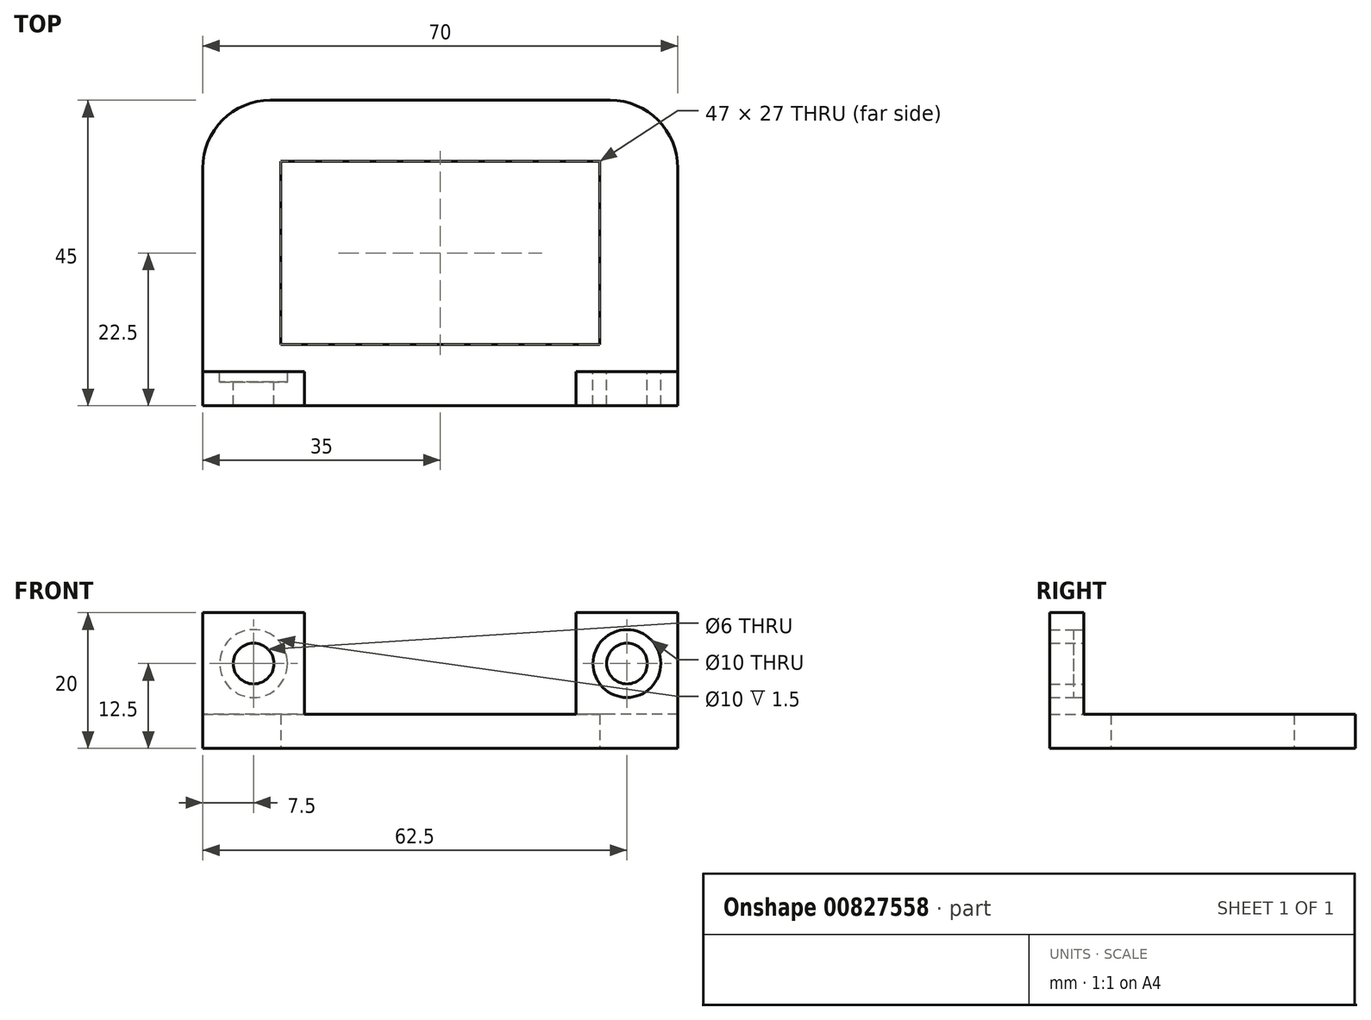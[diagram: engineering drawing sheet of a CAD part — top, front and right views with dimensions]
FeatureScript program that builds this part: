
annotation { "Feature Type Name" : "Feature", "Feature Type Description" : "" }
export const myFeature = defineFeature(function(context is Context, id is Id, definition is map)
    precondition{}
    {
        {
            var Q0;
            Q0=qCreatedBy(makeId("Top.planeOp"),FACE);
            var sketch = newSketch(context, id + "F0", { "sketchPlane" : qUnion([Q0])});
            skLineSegment(sketch, "E0.bottom", {"start": v(35, -22.5) * mm, "end": v(-35, -22.5) * mm});
            skLineSegment(sketch, "E0.top", {"start": v(25, 22.5) * mm, "end": v(-25, 22.5) * mm});
            skLineSegment(sketch, "E0.left", {"start": v(35, -22.5) * mm, "end": v(35, 12.5) * mm});
            skLineSegment(sketch, "E0.right", {"start": v(-35, -22.5) * mm, "end": v(-35, 12.5) * mm});
            skPoint(sketch, "E0.middle", {"position": v(0, 0) * mm});
            skPoint(sketch, "E1.visualSharp", {"position": v(35, 22.5) * mm});
            skArc(sketch, "E1.filletArc", {"start": v(35, 12.5) * mm, "mid": v(32.07, 19.57) * mm, "end": v(25, 22.5) * mm});
            skPoint(sketch, "E2.visualSharp", {"position": v(-35, 22.5) * mm});
            skArc(sketch, "E2.filletArc", {"start": v(-25, 22.5) * mm, "mid": v(-32.07, 19.57) * mm, "end": v(-35, 12.5) * mm});
            skSolve(sketch);
        }
        {
            var Q0;
            Q0 = qSketchRegion(id + "F0", true);
            extrude(context, id + "F1", {"entities" : qUnion([Q0]), "depth" : 5 * mm, "offsetDistance" : 25 * mm});
        }
        {
            var Q0;
            Q0=qCreatedBy(makeId("Top.planeOp"),FACE);
            var sketch = newSketch(context, id + "F2", { "sketchPlane" : qUnion([Q0])});
            skLineSegment(sketch, "E3.bottom", {"start": v(23.5, 13.5) * mm, "end": v(-23.5, 13.5) * mm});
            skLineSegment(sketch, "E3.top", {"start": v(23.5, -13.5) * mm, "end": v(-23.5, -13.5) * mm});
            skLineSegment(sketch, "E3.left", {"start": v(23.5, 13.5) * mm, "end": v(23.5, -13.5) * mm});
            skLineSegment(sketch, "E3.right", {"start": v(-23.5, 13.5) * mm, "end": v(-23.5, -13.5) * mm});
            skPoint(sketch, "E3.middle", {"position": v(0, 0) * mm});
            skSolve(sketch);
        }
        {
            var Q0;
            Q0 = qSketchRegion(id + "F2", true);
            extrude(context, id + "F3", {"entities" : qUnion([Q0]), "operationType" : NewBodyOperationType.REMOVE, "depth" : 25 * mm, "offsetDistance" : 25 * mm});
        }
        {
            var Q0;
            Q0=makeQuery(id+"F1.opExtrude","CAP_FACE",FACE,{"disambiguationData":[OSD([sQuery(id+"F0.wireOp",EDGE,"E0.bottom"),sQuery(id+"F0.wireOp",EDGE,"E0.top"),sQuery(id+"F0.wireOp",EDGE,"E0.left"),sQuery(id+"F0.wireOp",EDGE,"E0.right")])],"isStart":false});
            var sketch = newSketch(context, id + "F4", { "sketchPlane" : qUnion([Q0])});
            skLineSegment(sketch, "E4", {"start": v(0, 36.1) * mm, "end": v(0, -52.15) * mm, "construction": true});
            skLineSegment(sketch, "E5.bottom", {"start": v(-35, -22.5) * mm, "end": v(-20, -22.5) * mm});
            skLineSegment(sketch, "E5.top", {"start": v(-35, -17.5) * mm, "end": v(-20, -17.5) * mm});
            skLineSegment(sketch, "E5.left", {"start": v(-35, -22.5) * mm, "end": v(-35, -17.5) * mm});
            skLineSegment(sketch, "E5.right", {"start": v(-20, -22.5) * mm, "end": v(-20, -17.5) * mm});
            skLineSegment(sketch, "E6.bottom", {"start": v(35, -22.5) * mm, "end": v(20, -22.5) * mm});
            skLineSegment(sketch, "E6.top", {"start": v(35, -17.5) * mm, "end": v(20, -17.5) * mm});
            skLineSegment(sketch, "E6.left", {"start": v(35, -22.5) * mm, "end": v(35, -17.5) * mm});
            skLineSegment(sketch, "E6.right", {"start": v(20, -22.5) * mm, "end": v(20, -17.5) * mm});
            skSolve(sketch);
        }
        {
            var Q0;
            Q0 = qSketchRegion(id + "F4", true);
            extrude(context, id + "F5", {"entities" : qUnion([Q0]), "operationType" : NewBodyOperationType.ADD, "depth" : 15 * mm, "offsetDistance" : 25 * mm});
        }
        {
            var Q0;
            Q0=makeQuery(id+"F5.opExtrude","SWEPT_FACE",FACE,{"disambiguationData":[OSD([sQuery(id+"F4.wireOp",EDGE,"E5.top")])]});
            var sketch = newSketch(context, id + "F6", { "sketchPlane" : qUnion([Q0])});
            skLineSegment(sketch, "E7", {"start": v(0, -17.9) * mm, "end": v(0, 34.22) * mm, "construction": true});
            skLineSegment(sketch, "E8", {"start": v(35, 20) * mm, "end": v(20, 5) * mm, "construction": true});
            skCircle(sketch, "E9", {"center": v(27.5, 12.5) * mm, "radius": 3 * mm});
            skCircle(sketch, "E10", {"center": v(27.5, 12.5) * mm, "radius": 5 * mm});
            skCircle(sketch, "E11.MirrorC", {"center": v(-27.5, 12.5) * mm, "radius": 3 * mm});
            skCircle(sketch, "E12.MirrorC", {"center": v(-27.5, 12.5) * mm, "radius": 5 * mm});
            skSolve(sketch);
        }
        {
            var Q0;
            Q0=makeQuery(id+"F6.imprint","IMPRINT",FACE,{"disambiguationData":[TD([[makeQuery(id+"F6.imprint","IMPRINT",EDGE,{"derivedFrom":sQuery(id+"F6.wireOp",EDGE,"E9")}),1.0]])]});
            var Q1;
            Q1=makeQuery(id+"F6.imprint","IMPRINT",FACE,{"disambiguationData":[TD([[makeQuery(id+"F6.imprint","IMPRINT",EDGE,{"derivedFrom":sQuery(id+"F6.wireOp",EDGE,"E11.MirrorC")}),-1.0]])]});
            extrude(context, id + "F7", {"entities" : qUnion([Q0, Q1]), "operationType" : NewBodyOperationType.REMOVE, "oppositeDirection" : true, "depth" : 25 * mm, "offsetDistance" : 25 * mm});
        }
        {
            var Q0;
            Q0 = qSketchRegion(id + "F6", true);
            extrude(context, id + "F8", {"entities" : qUnion([Q0]), "operationType" : NewBodyOperationType.REMOVE, "oppositeDirection" : true, "depth" : 1.5 * mm, "offsetDistance" : 25 * mm});
        }
    });
